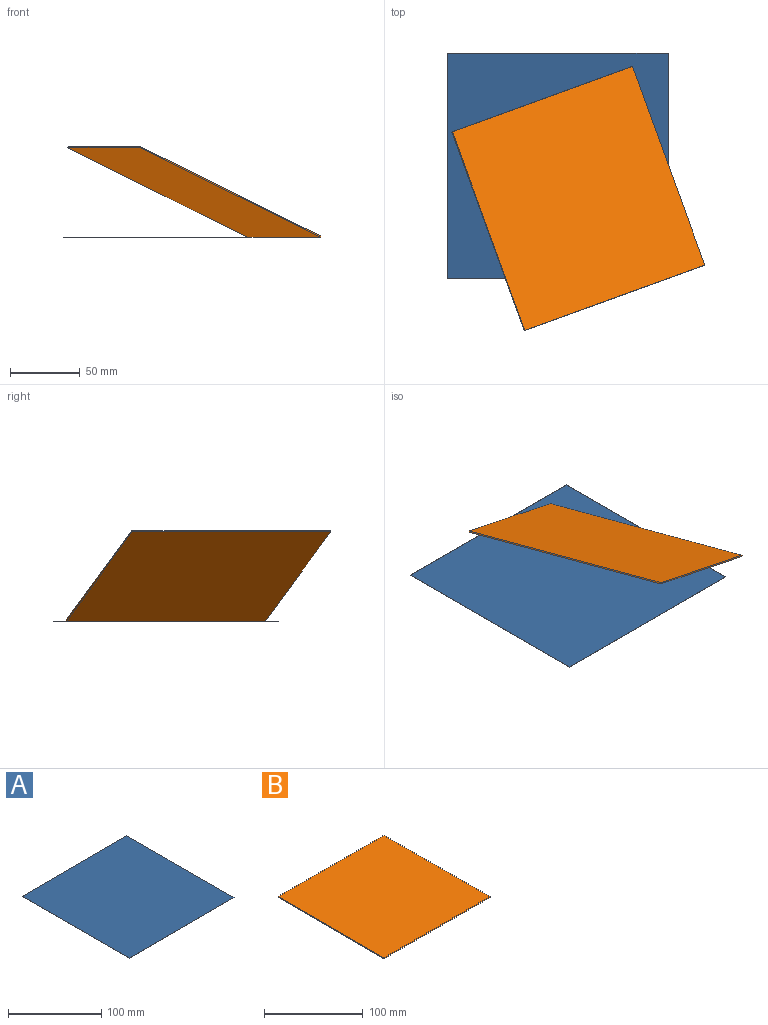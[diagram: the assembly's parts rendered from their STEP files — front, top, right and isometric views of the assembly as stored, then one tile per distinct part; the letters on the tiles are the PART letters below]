
ASSEMBLY  parts=2 mates=1
PART A: 6 faces, bbox 158.9x162x0.2 mm
  f0: plane 162x0.15mm, normal (1,0,0), area 24.3mm2, adj f1,f3,f4,f5
  f1: plane 158.87x0.15mm, normal (0,1,0), area 23.8mm2, adj f0,f2,f4,f5
  f2: plane 162x0.15mm, normal (-1,0,0), area 24.3mm2, adj f1,f3,f4,f5
  f3: plane 158.87x0.15mm, normal (0,-1,0), area 23.8mm2, adj f0,f2,f4,f5
  f4: plane 162x158.87mm, normal (0,0,-1), area 25736.4mm2, adj f0,f1,f2,f3
  f5: plane 162x158.87mm, normal (0,0,1), area 25736.4mm2, adj f0,f1,f2,f3
PART B: 6 faces, bbox 152x152x1 mm
  f0: plane 152x1mm, normal (1,0,0), area 152mm2, adj f1,f3,f4,f5
  f1: plane 152x1mm, normal (0,1,0), area 152mm2, adj f0,f2,f4,f5
  f2: plane 152x1mm, normal (-1,0,0), area 152mm2, adj f1,f3,f4,f5
  f3: plane 152x1mm, normal (0,-1,0), area 152mm2, adj f0,f2,f4,f5
  f4: plane 152x152mm, normal (0,0,1), area 23104mm2, adj f0,f1,f2,f3
  f5: plane 152x152mm, normal (0,0,-1), area 23104mm2, adj f0,f1,f2,f3
PLACE A t=(-14.43,41.73,-56.19)mm
PLACE B rot(axis=(-0.14,0.78,0.62),31.9deg) t=(0.28,18.17,-24.07)mm
MATE ball B.f0 <-> A.f0  axis (0.85,0.31,-0.42) through (65.01,41.73,-56.19)mm
